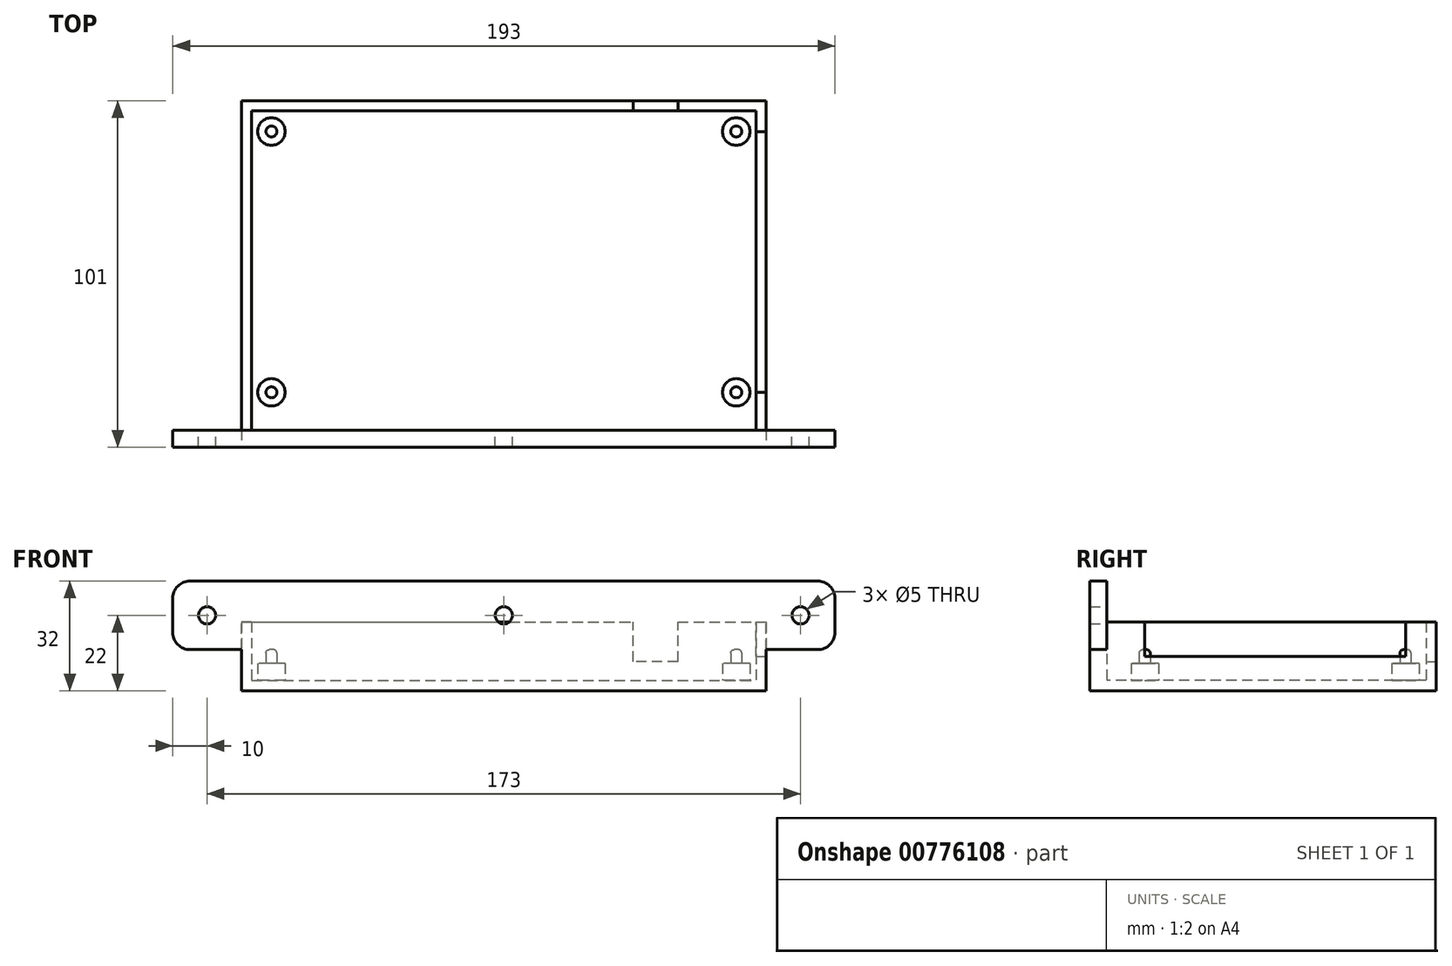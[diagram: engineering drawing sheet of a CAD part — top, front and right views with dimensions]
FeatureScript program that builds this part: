
annotation { "Feature Type Name" : "Feature", "Feature Type Description" : "" }
export const myFeature = defineFeature(function(context is Context, id is Id, definition is map)
    precondition{}
    {
        {
            var Q0;
            Q0=qCreatedBy(makeId("Top.planeOp"),FACE);
            var sketch = newSketch(context, id + "F0", { "sketchPlane" : qUnion([Q0])});
            skLineSegment(sketch, "E0.bottom", {"start": v(71.5, -42) * mm, "end": v(-71.5, -42) * mm, "construction": true});
            skLineSegment(sketch, "E0.top", {"start": v(71.5, 42) * mm, "end": v(-71.5, 42) * mm, "construction": true});
            skLineSegment(sketch, "E0.left", {"start": v(71.5, -42) * mm, "end": v(71.5, 42) * mm, "construction": true});
            skLineSegment(sketch, "E0.right", {"start": v(-71.5, -42) * mm, "end": v(-71.5, 42) * mm, "construction": true});
            skPoint(sketch, "E0.middle", {"position": v(0, 0) * mm});
            skLineSegment(sketch, "E1.bottom", {"start": v(67.75, -38) * mm, "end": v(-67.75, -38) * mm, "construction": true});
            skLineSegment(sketch, "E1.top", {"start": v(67.75, 38) * mm, "end": v(-67.75, 38) * mm, "construction": true});
            skLineSegment(sketch, "E1.left", {"start": v(67.75, -38) * mm, "end": v(67.75, 38) * mm, "construction": true});
            skLineSegment(sketch, "E1.right", {"start": v(-67.75, -38) * mm, "end": v(-67.75, 38) * mm, "construction": true});
            skLineSegment(sketch, "E2.bottom", {"start": v(-76.5, 47) * mm, "end": v(76.5, 47) * mm});
            skLineSegment(sketch, "E2.top", {"start": v(-76.5, -52) * mm, "end": v(76.5, -52) * mm});
            skLineSegment(sketch, "E2.left", {"start": v(-76.5, 47) * mm, "end": v(-76.5, -52) * mm});
            skLineSegment(sketch, "E2.right", {"start": v(76.5, 47) * mm, "end": v(76.5, -52) * mm});
            skCircle(sketch, "E3", {"center": v(-67.75, 38) * mm, "radius": 4 * mm});
            skCircle(sketch, "E4", {"center": v(67.75, 38) * mm, "radius": 4 * mm});
            skCircle(sketch, "E5", {"center": v(-67.75, -38) * mm, "radius": 4 * mm});
            skCircle(sketch, "E6", {"center": v(67.75, -38) * mm, "radius": 4 * mm});
            skSolve(sketch);
        }
        {
            var Q0;
            Q0 = qSketchRegion(id + "F0", true);
            var Q1;
            Q1=makeQuery(id+"F0.imprint","IMPRINT",FACE,{"disambiguationData":[TD([[makeQuery(id+"F0.imprint","IMPRINT",EDGE,{"derivedFrom":sQuery(id+"F0.wireOp",EDGE,"E3")}),1.0]])]});
            var Q2;
            Q2=makeQuery(id+"F0.imprint","IMPRINT",FACE,{"disambiguationData":[TD([[makeQuery(id+"F0.imprint","IMPRINT",EDGE,{"derivedFrom":sQuery(id+"F0.wireOp",EDGE,"E5")}),1.0]])]});
            var Q3;
            Q3=makeQuery(id+"F0.imprint","IMPRINT",FACE,{"disambiguationData":[TD([[makeQuery(id+"F0.imprint","IMPRINT",EDGE,{"derivedFrom":sQuery(id+"F0.wireOp",EDGE,"E6")}),1.0]])]});
            var Q4;
            Q4=makeQuery(id+"F0.imprint","IMPRINT",FACE,{"disambiguationData":[TD([[makeQuery(id+"F0.imprint","IMPRINT",EDGE,{"derivedFrom":sQuery(id+"F0.wireOp",EDGE,"E4")}),1.0]])]});
            extrude(context, id + "F1", {"entities" : qUnion([Q0, Q1, Q2, Q3, Q4]), "depth" : 20 * mm, "offsetDistance" : 25 * mm});
        }
        {
            var Q0;
            Q0=makeQuery(id+"F1.opExtrude","CAP_FACE",FACE,{"disambiguationData":[OSD([sQuery(id+"F0.wireOp",EDGE,"E2.bottom"),sQuery(id+"F0.wireOp",EDGE,"E2.top"),sQuery(id+"F0.wireOp",EDGE,"E2.left"),sQuery(id+"F0.wireOp",EDGE,"E2.right")])],"isStart":false});
            shell(context, id + "F2", {"entities" : qUnion([Q0]), "thickness" : 3 * mm});
        }
        {
            var Q0;
            Q0=makeQuery(id+"F2.opShell","OFFSET_FACE",FACE,{"disambiguationData":[OSD([sQuery(id+"F0.wireOp",EDGE,"E2.bottom"),sQuery(id+"F0.wireOp",EDGE,"E2.top"),sQuery(id+"F0.wireOp",EDGE,"E2.left"),sQuery(id+"F0.wireOp",EDGE,"E2.right")])]});
            var sketch = newSketch(context, id + "F3", { "sketchPlane" : qUnion([Q0])});
            skCircle(sketch, "E7.0", {"center": v(-67.75, 38) * mm, "radius": 4 * mm});
            skCircle(sketch, "E8.0", {"center": v(-67.75, -38) * mm, "radius": 4 * mm});
            skCircle(sketch, "E9.0", {"center": v(67.75, 38) * mm, "radius": 4 * mm});
            skCircle(sketch, "E10.0", {"center": v(67.75, -38) * mm, "radius": 4 * mm});
            skSolve(sketch);
        }
        {
            var Q0;
            Q0=makeQuery(id+"F3.imprint","IMPRINT",FACE,{"disambiguationData":[TD([[makeQuery(id+"F3.imprint","IMPRINT",EDGE,{"derivedFrom":sQuery(id+"F3.wireOp",EDGE,"E7.0")}),1.0]])]});
            var Q1;
            Q1=makeQuery(id+"F3.imprint","IMPRINT",FACE,{"disambiguationData":[TD([[makeQuery(id+"F3.imprint","IMPRINT",EDGE,{"derivedFrom":sQuery(id+"F3.wireOp",EDGE,"E8.0")}),1.0]])]});
            var Q2;
            Q2=makeQuery(id+"F3.imprint","IMPRINT",FACE,{"disambiguationData":[TD([[makeQuery(id+"F3.imprint","IMPRINT",EDGE,{"derivedFrom":sQuery(id+"F3.wireOp",EDGE,"E9.0")}),1.0]])]});
            var Q3;
            Q3=makeQuery(id+"F3.imprint","IMPRINT",FACE,{"disambiguationData":[TD([[makeQuery(id+"F3.imprint","IMPRINT",EDGE,{"derivedFrom":sQuery(id+"F3.wireOp",EDGE,"E10.0")}),1.0]])]});
            extrude(context, id + "F4", {"entities" : qUnion([Q0, Q1, Q2, Q3]), "operationType" : NewBodyOperationType.ADD, "depth" : 5 * mm, "offsetDistance" : 25 * mm});
        }
        {
            var Q0;
            Q0=makeQuery(id+"F4.opExtrude","CAP_FACE",FACE,{"disambiguationData":[OSD([sQuery(id+"F3.wireOp",EDGE,"E8.0")])],"isStart":false});
            var sketch = newSketch(context, id + "F5", { "sketchPlane" : qUnion([Q0])});
            skCircle(sketch, "E11.0", {"center": v(-67.75, 38) * mm, "radius": 4 * mm});
            skCircle(sketch, "E12.0", {"center": v(67.75, 38) * mm, "radius": 4 * mm});
            skCircle(sketch, "E13.0", {"center": v(67.75, -38) * mm, "radius": 4 * mm});
            skCircle(sketch, "E14", {"center": v(-67.75, -38) * mm, "radius": 1.6 * mm});
            skCircle(sketch, "E15", {"center": v(-67.75, 38) * mm, "radius": 1.6 * mm});
            skCircle(sketch, "E16", {"center": v(67.75, 38) * mm, "radius": 1.6 * mm});
            skCircle(sketch, "E17", {"center": v(67.75, -38) * mm, "radius": 1.6 * mm});
            skSolve(sketch);
        }
        {
            var Q0;
            Q0=makeQuery(id+"F5.imprint","IMPRINT",FACE,{"disambiguationData":[TD([[makeQuery(id+"F5.imprint","IMPRINT",EDGE,{"derivedFrom":sQuery(id+"F5.wireOp",EDGE,"E14")}),1.0]])]});
            var Q1;
            Q1=makeQuery(id+"F5.imprint","IMPRINT",FACE,{"disambiguationData":[TD([[makeQuery(id+"F5.imprint","IMPRINT",EDGE,{"derivedFrom":sQuery(id+"F5.wireOp",EDGE,"E15")}),1.0]])]});
            var Q2;
            Q2=makeQuery(id+"F5.imprint","IMPRINT",FACE,{"disambiguationData":[TD([[makeQuery(id+"F5.imprint","IMPRINT",EDGE,{"derivedFrom":sQuery(id+"F5.wireOp",EDGE,"E16")}),1.0]])]});
            var Q3;
            Q3=makeQuery(id+"F5.imprint","IMPRINT",FACE,{"disambiguationData":[TD([[makeQuery(id+"F5.imprint","IMPRINT",EDGE,{"derivedFrom":sQuery(id+"F5.wireOp",EDGE,"E17")}),1.0]])]});
            extrude(context, id + "F6", {"entities" : qUnion([Q0, Q1, Q2, Q3]), "operationType" : NewBodyOperationType.ADD, "depth" : 4 * mm, "offsetDistance" : 25 * mm});
        }
        {
            var Q0;
            Q0=makeQuery(id+"F6.opExtrude","CAP_EDGE",EDGE,{"disambiguationData":[OSD([sQuery(id+"F5.wireOp",EDGE,"E15")])],"isStart":false});
            var Q1;
            Q1=makeQuery(id+"F6.opExtrude","CAP_EDGE",EDGE,{"disambiguationData":[OSD([sQuery(id+"F5.wireOp",EDGE,"E14")])],"isStart":false});
            var Q2;
            Q2=makeQuery(id+"F6.opExtrude","CAP_EDGE",EDGE,{"disambiguationData":[OSD([sQuery(id+"F5.wireOp",EDGE,"E16")])],"isStart":false});
            var Q3;
            Q3=makeQuery(id+"F6.opExtrude","CAP_EDGE",EDGE,{"disambiguationData":[OSD([sQuery(id+"F5.wireOp",EDGE,"E17")])],"isStart":false});
            fillet(context, id + "F7", {"entities" : qUnion([Q0, Q1, Q2, Q3]), "tangentPropagation" : true, "radius" : 1 * mm, "defaultsChanged" : true, "vertexSettings" : [], "allowEdgeOverflow" : false});
        }
        {
            var Q0;
            Q0=makeQuery(id+"F1.opExtrude","SWEPT_FACE",FACE,{"disambiguationData":[OSD([sQuery(id+"F0.wireOp",EDGE,"E2.top")])]});
            var sketch = newSketch(context, id + "F8", { "sketchPlane" : qUnion([Q0])});
            skLineSegment(sketch, "E18.bottom", {"start": v(-96.5, 32) * mm, "end": v(96.5, 32) * mm});
            skLineSegment(sketch, "E18.top", {"start": v(-96.5, 12) * mm, "end": v(96.5, 12) * mm});
            skLineSegment(sketch, "E18.left", {"start": v(-96.5, 32) * mm, "end": v(-96.5, 12) * mm});
            skLineSegment(sketch, "E18.right", {"start": v(96.5, 32) * mm, "end": v(96.5, 12) * mm});
            skPoint(sketch, "E19", {"position": v(-96.5, 22) * mm});
            skPoint(sketch, "E20", {"position": v(-86.5, 22) * mm});
            skPoint(sketch, "E21", {"position": v(86.5, 22) * mm});
            skPoint(sketch, "E21.positionSnap0", {"position": v(96.5, 22) * mm});
            skPoint(sketch, "E22", {"position": v(0, 22) * mm});
            skLineSegment(sketch, "E23.bottom", {"start": v(-76.5, 20) * mm, "end": v(76.5, 20) * mm});
            skLineSegment(sketch, "E23.top", {"start": v(-76.5, 0) * mm, "end": v(76.5, 0) * mm});
            skLineSegment(sketch, "E23.left", {"start": v(-76.5, 20) * mm, "end": v(-76.5, 0) * mm});
            skLineSegment(sketch, "E23.right", {"start": v(76.5, 20) * mm, "end": v(76.5, 0) * mm});
            skSolve(sketch);
        }
        {
            var Q0;
            Q0 = qSketchRegion(id + "F8", true);
            var Q1;
            Q1=makeQuery(id+"F2.opShell","OFFSET_FACE",FACE,{"disambiguationData":[OSD([sQuery(id+"F0.wireOp",EDGE,"E2.top")])]});
            extrude(context, id + "F9", {"entities" : qUnion([Q0]), "operationType" : NewBodyOperationType.ADD, "endBound" : BoundingType.UP_TO_SURFACE, "oppositeDirection" : true, "depth" : 25 * mm, "endBoundEntityFace" : qUnion([Q1]), "offsetDistance" : 25 * mm, "hasSecondDirection" : true, "secondDirectionOppositeDirection" : false, "secondDirectionDepth" : 2 * mm});
        }
        {
            var Q0;
            Q0=makeQuery(id+"F9.opExtrude","SWEPT_EDGE",EDGE,{"disambiguationData":[OSD([sQuery(id+"F8.wireOp",EDGE,"E18.bottom"),sQuery(id+"F8.wireOp",EDGE,"E18.left")])]});
            var Q1;
            Q1=makeQuery(id+"F9.opExtrude","SWEPT_EDGE",EDGE,{"disambiguationData":[OSD([sQuery(id+"F8.wireOp",EDGE,"E18.top"),sQuery(id+"F8.wireOp",EDGE,"E18.left")])]});
            var Q2;
            Q2=makeQuery(id+"F9.opExtrude","SWEPT_EDGE",EDGE,{"disambiguationData":[OSD([sQuery(id+"F8.wireOp",EDGE,"E18.bottom"),sQuery(id+"F8.wireOp",EDGE,"E18.right")])]});
            var Q3;
            Q3=makeQuery(id+"F9.opExtrude","SWEPT_EDGE",EDGE,{"disambiguationData":[OSD([sQuery(id+"F8.wireOp",EDGE,"E18.top"),sQuery(id+"F8.wireOp",EDGE,"E18.right")])]});
            fillet(context, id + "F10", {"entities" : qUnion([Q0, Q1, Q2, Q3]), "tangentPropagation" : true, "radius" : 5 * mm, "defaultsChanged" : false, "vertexSettings" : [], "allowEdgeOverflow" : false});
        }
        {
            var Q0;
            Q0=makeQuery(id+"F1.opExtrude","SWEPT_FACE",FACE,{"disambiguationData":[OSD([sQuery(id+"F0.wireOp",EDGE,"E2.bottom")])]});
            var sketch = newSketch(context, id + "F11", { "sketchPlane" : qUnion([Q0])});
            skPoint(sketch, "E24.0", {"position": v(-67.75, 8) * mm});
            skPoint(sketch, "E25", {"position": v(-67.75, 8.5) * mm});
            skPoint(sketch, "E26", {"position": v(-50.75, 8.5) * mm});
            skLineSegment(sketch, "E27.bottom", {"start": v(-50.75, 8.5) * mm, "end": v(-37.75, 8.5) * mm});
            skLineSegment(sketch, "E27.top", {"start": v(-50.75, 21.5) * mm, "end": v(-37.75, 21.5) * mm});
            skLineSegment(sketch, "E27.left", {"start": v(-50.75, 8.5) * mm, "end": v(-50.75, 21.5) * mm});
            skLineSegment(sketch, "E27.right", {"start": v(-37.75, 8.5) * mm, "end": v(-37.75, 21.5) * mm});
            skSolve(sketch);
        }
        {
            var Q0;
            {var subQ0=sQuery(id+"F11.wireOp",EDGE,"E27.bottom");Q0=makeQuery(id+"F11.imprint","IMPRINT",FACE,{"disambiguationData":[TD([[makeQuery(id+"F11.imprint","IMPRINT",EDGE,{"derivedFrom":subQ0}),1.0]])]});}
            extrude(context, id + "F12", {"entities" : qUnion([Q0]), "operationType" : NewBodyOperationType.REMOVE, "endBound" : BoundingType.UP_TO_NEXT, "oppositeDirection" : true, "depth" : 25 * mm, "offsetDistance" : 25 * mm});
        }
        {
            var Q0;
            Q0=makeQuery(id+"F1.opExtrude","SWEPT_FACE",FACE,{"disambiguationData":[OSD([sQuery(id+"F0.wireOp",EDGE,"E2.left")])]});
            var sketch = newSketch(context, id + "F13", { "sketchPlane" : qUnion([Q0])});
            skPoint(sketch, "E28.0", {"position": v(-38, 8) * mm});
            skPoint(sketch, "E29", {"position": v(-33, 8) * mm});
            skPoint(sketch, "E30", {"position": v(-33, 19) * mm});
            skLineSegment(sketch, "E31.bottom", {"start": v(-33, 19) * mm, "end": v(11, 19) * mm});
            skLineSegment(sketch, "E31.top", {"start": v(-33, 29) * mm, "end": v(11, 29) * mm});
            skLineSegment(sketch, "E31.left", {"start": v(-33, 19) * mm, "end": v(-33, 29) * mm});
            skLineSegment(sketch, "E31.right", {"start": v(11, 19) * mm, "end": v(11, 29) * mm});
            skSolve(sketch);
        }
        {
            var Q0;
            Q0=makeQuery(id+"F1.opExtrude","SWEPT_FACE",FACE,{"disambiguationData":[OSD([sQuery(id+"F0.wireOp",EDGE,"E2.right")])]});
            var sketch = newSketch(context, id + "F14", { "sketchPlane" : qUnion([Q0])});
            skPoint(sketch, "E32.0", {"position": v(-38, 8) * mm});
            skPoint(sketch, "E33.0", {"position": v(38, 8) * mm});
            skLineSegment(sketch, "E34.bottom", {"start": v(-38, 20) * mm, "end": v(38, 20) * mm});
            skLineSegment(sketch, "E34.top", {"start": v(-38, 10) * mm, "end": v(38, 10) * mm});
            skLineSegment(sketch, "E34.left", {"start": v(-38, 20) * mm, "end": v(-38, 10) * mm});
            skLineSegment(sketch, "E34.right", {"start": v(38, 20) * mm, "end": v(38, 10) * mm});
            skSolve(sketch);
        }
        {
            var Q0;
            Q0 = qSketchRegion(id + "F14", true);
            extrude(context, id + "F15", {"entities" : qUnion([Q0]), "operationType" : NewBodyOperationType.REMOVE, "endBound" : BoundingType.UP_TO_NEXT, "oppositeDirection" : true, "depth" : 25 * mm, "offsetDistance" : 25 * mm});
        }
        {
            var Q0;
            Q0=makeQuery(id+"F9.opExtrude","CAP_FACE",FACE,{"disambiguationData":[OSD([sQuery(id+"F8.wireOp",EDGE,"E18.bottom"),sQuery(id+"F8.wireOp",EDGE,"E18.top"),sQuery(id+"F8.wireOp",EDGE,"E18.left"),sQuery(id+"F8.wireOp",EDGE,"E18.right"),sQuery(id+"F8.wireOp",EDGE,"E23.top"),sQuery(id+"F8.wireOp",EDGE,"E23.left"),sQuery(id+"F8.wireOp",EDGE,"E23.right")])],"isStart":true});
            var sketch = newSketch(context, id + "F16", { "sketchPlane" : qUnion([Q0])});
            skPoint(sketch, "E35.0", {"position": v(-86.5, 22) * mm});
            skPoint(sketch, "E36.0", {"position": v(0, 22) * mm});
            skPoint(sketch, "E37.0", {"position": v(86.5, 22) * mm});
            skSolve(sketch);
        }
        {
            var Q0;
            Q0=sQuery(id+"F16.wireOp",VERTEX,"E35.0");
            var Q1;
            Q1=sQuery(id+"F16.wireOp",VERTEX,"E36.0");
            var Q2;
            Q2=sQuery(id+"F16.wireOp",VERTEX,"E37.0");
            var Q3;
            Q3=makeQuery(id+"F1.opExtrude","SWEPT_BODY",BODY,{"disambiguationData":[OSD([sQuery(id+"F0.wireOp",EDGE,"E2.bottom"),sQuery(id+"F0.wireOp",EDGE,"E2.top"),sQuery(id+"F0.wireOp",EDGE,"E2.left"),sQuery(id+"F0.wireOp",EDGE,"E2.right")])]});
            hole(context, id + "F17", {"style" : HoleStyle.SIMPLE, "endStyle" : HoleEndStyle.BLIND, "holeDiameter" : 5 * mm, "majorDiameter" : 5 * mm, "holeDepth" : 6 * mm, "isTappedThrough" : true, "tappedDepth" : 12 * mm, "tapClearance" : 3, "locations" : qUnion([Q0, Q1, Q2]), "scope" : qUnion([Q3])});
        }
    });
